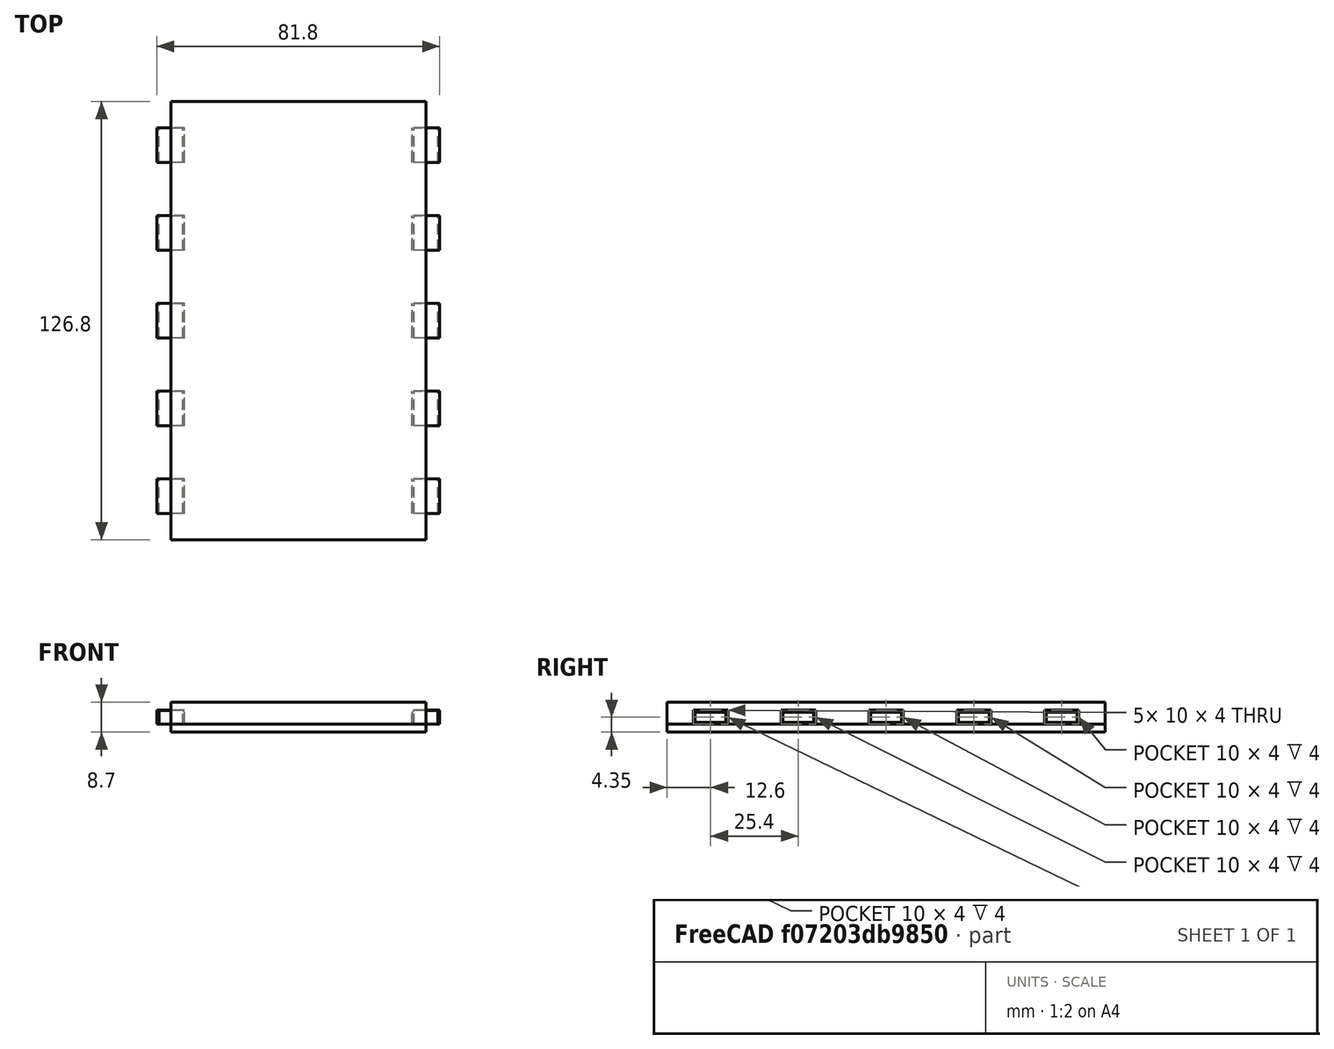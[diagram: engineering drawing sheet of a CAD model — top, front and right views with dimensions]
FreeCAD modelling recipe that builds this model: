
FCSTD DOCUMENT  (FreeCAD 0.21R33771 (Git))
Label: Spacers
Comment: <copyright redacted>\n\nPermission is hereby granted, free of charge, to any person obtaining a copy\nof this software and associated documentation files (the "Software"), to deal\nin the S... (+873 chars)
License: All rights reserved
LicenseURL: https://en.wikipedia.org/wiki/MIT_License
objects: PartDesign::AdditiveBox×3, PartDesign::Body×3, Part::FeaturePython×2, PartDesign::Boolean×2, Spreadsheet::Sheet×1, Part::Box×1, PartDesign::Chamfer×1, PartDesign::FeatureBase×1, PartDesign::SubtractiveBox×1
note: 19 computed .brp shape members not serialized (recipe doc carries the construction recipe); baked Part::Feature solids carry a one-line shape summary decoded from their .brp

FEATURE [Spreadsheet::Sheet] Spreadsheet  label="$params"
  cells = A1='name; B1='value; C1='description; E1='internal name; F1='computed value; G1='description; A2='count_x; B2(count_x)=3; C2='Number of spans (left/right) on pegboard; E2='size_x; F2(size_x)==(count_x - 1) * pin_spacing + single_width; A3='count_y; B3(count_y)=5; C3='Number of spans (up/down) on pegboard. Also number of pins on each side.; E3='size_y; F3(size_y)==(count_y - 1) * pin_spacing + pin_nominal_length + 2 * pin_to_edge_length; A6='Common Constants; A7='flush_height; B7(flush_height)=8.7; C7='How far out from the pegboard is "flush" / "flat"; A8='single_width; B8(single_width)=23; C8='Width of a 1x1 piece (Left/Right on the pegboard); A13='4mmx8mmx10mm Pin Constants; A14='pin_nominal_length; B14(pin_nominal_length)=10; C14='Up/down on the pegboard; E14='pin_length; F14(pin_length)==pin_nominal_length - pin_clearance; A15='pin_nominal_width; B15(pin_nominal_width)=8; C15='Left/Right on the pegboard; E15='pin_width; F15(pin_width)==pin_nominal_width - pin_clearance; A16='pin_nominal_height; B16(pin_nominal_height)=4; C16='Out from the pegboard; E16='pin_height; F16(pin_height)==pin_nominal_height - pin_clearance; A17='pin_clearance; B17(pin_clearance)=0.1; C17='Difference between nominal and actual value (length, width, height); A18='pin_spacing; B18(pin_spacing)=25.4; C18='Distance between pin center points (up/down on the pegboard); A19='pin_to_edge_length; B19(pin_to_edge_length)=7.6; C19='Distance from the edge of a pin to the edge of the part (up/down on pegbaord); A24=1; B24=23; A25=2; B25=48.4; C25==23 + pin_spacing; A26=3; B26=73.8
FEATURE [Part::Box] Box001  label="Nominal 4x8x10 Pin"
  AttacherType = Attacher::AttachEngine3D
  AttachmentOffset = pos=(4,7.6,2.35) rot=(0,0,1;1.5708rad)
  Height = 4
  Length = 10
  MapMode = 5
  Placement = pos=(4,7.6,2.35) rot=(0,0,1;1.5708rad)
  Support = -> [XY_Plane006]
  Width = 8
  expr: .AttachmentOffset.Base.x = Width / 2
  expr: .AttachmentOffset.Base.y = Spreadsheet.pin_to_edge_length
  expr: .AttachmentOffset.Base.z = <<$params>>.flush_height / 2 - <<$params>>.pin_nominal_height / 2
  expr: Height = <<$params>>.pin_nominal_height
  expr: Length = <<$params>>.pin_nominal_length
  expr: Width = <<$params>>.pin_nominal_width
FEATURE [Part::FeaturePython] Array  # Draft array (typed FeaturePython)
  Angle = 360
  ArrayType = 0
  Axis = (0,0,1)
  Base = -> Box001
  Center = (0,0,0)
  Count = 10
  Fuse = true
  IntervalAxis = (0,0,0)
  IntervalX = (73.8,0,0)
  IntervalY = (0,25.4,0)
  IntervalZ = (0,0,0)
  NumberCircles = 3
  NumberPolar = 5
  NumberX = 2
  NumberY = 5
  NumberZ = 1
  RadialDistance = 50
  Symmetry = 1
  TangentialDistance = 25
  expr: .IntervalX.x = <<$params>>.size_x
  expr: .IntervalY.y = Spreadsheet.pin_spacing
  expr: NumberY = <<$params>>.count_y
FEATURE [PartDesign::AdditiveBox] Box003  label="Solid Body"
  AttacherType = Attacher::AttachEngine3D
  Height = 8.7
  Length = 73.8
  MapMode = 5
  Support = -> [XY_Plane006]
  Width = 126.8
  expr: Height = <<$params>>.flush_height
  expr: Length = <<$params>>.size_x
  expr: Width = <<$params>>.size_y
FEATURE [PartDesign::AdditiveBox] Box
  AttacherType = Attacher::AttachEngine3D
  Height = 3.9
  Length = 9.9
  MapMode = 5
  Support = -> [XY_Plane007]
  Width = 7.9
  expr: Height = <<$params>>.pin_height
  expr: Length = <<$params>>.pin_length
  expr: Width = <<$params>>.pin_width
FEATURE [PartDesign::Chamfer] Chamfer001
  Angle = 45
  Base = -> Box [Face3,Face4]
  BaseFeature = -> Box
  ChamferType = 0
  FlipDirection = false
  Size = 0.5
  Size2 = 1
  SupportTransform = false
  UseAllEdges = false
FEATURE [PartDesign::Body] Body004  label="4mmx8mmx10mm Pin"
  Group = -> [Box,Chamfer001]
  Origin = -> Origin006
  Tip = -> Chamfer001
FEATURE [PartDesign::Boolean] Boolean
  BaseFeature = -> Box003
  Group = -> [Box001,Array]
  Type = 1
FEATURE [PartDesign::Body] Body003  label="Blank Spacer Flush"
  Group = -> [Box003,Boolean]
  Origin = -> Origin005
  Tip = -> Boolean
FEATURE [PartDesign::AdditiveBox] Box004  label="Solid Body001"
  AttacherType = Attacher::AttachEngine3D
  Height = 8.7
  Length = 73.8
  MapMode = 5
  Support = -> [XY_Plane009]
  Width = 126.8
  expr: Height = <<$params>>.flush_height
  expr: Length = <<$params>>.size_x
  expr: Width = <<$params>>.size_y
FEATURE [PartDesign::FeatureBase] Clone  label="Clone of 4mmx8mmx10mm Pin"
  BaseFeature = -> Body004
  Placement = pos=(4,7.6,2.35) rot=(0,0,1;1.5708rad)
  expr: .Placement.Base.x = <<$params>>.pin_nominal_width / 2
  expr: .Placement.Base.y = Spreadsheet.pin_to_edge_length
  expr: .Placement.Base.z = <<$params>>.flush_height / 2 - <<$params>>.pin_nominal_height / 2
FEATURE [Part::FeaturePython] Array001  # Draft array (typed FeaturePython)
  Angle = 360
  ArrayType = 0
  Axis = (0,0,1)
  Base = -> Clone
  Center = (0,0,0)
  Count = 10
  Fuse = true
  IntervalAxis = (0,0,0)
  IntervalX = (73.8,0,0)
  IntervalY = (0,25.4,0)
  IntervalZ = (0,0,100)
  NumberCircles = 3
  NumberPolar = 5
  NumberX = 2
  NumberY = 5
  NumberZ = 1
  RadialDistance = 50
  Symmetry = 1
  TangentialDistance = 25
  expr: .IntervalX.x = <<$params>>.size_x
  expr: .IntervalY.y = Spreadsheet.pin_spacing
  expr: NumberY = <<$params>>.count_y
FEATURE [PartDesign::Boolean] Boolean001
  BaseFeature = -> Box004
  Group = -> [Clone,Array001]
  Type = 0
FEATURE [PartDesign::SubtractiveBox] Box005
  AttacherType = Attacher::AttachEngine3D
  BaseFeature = -> Boolean001
  Height = 2.35
  Length = 73.8
  MapMode = 2
  Support = -> [Box004]
  Width = 126.8
  expr: Height = <<$params>>.flush_height / 2 - <<$params>>.pin_nominal_height / 2
  expr: Length = <<$params>>.size_x
  expr: Width = <<$params>>.size_y
FEATURE [PartDesign::Body] Body006  label="Blank Spacer"
  Group = -> [Box004,Boolean001,Box005]
  Origin = -> Origin008
  Tip = -> Box005
